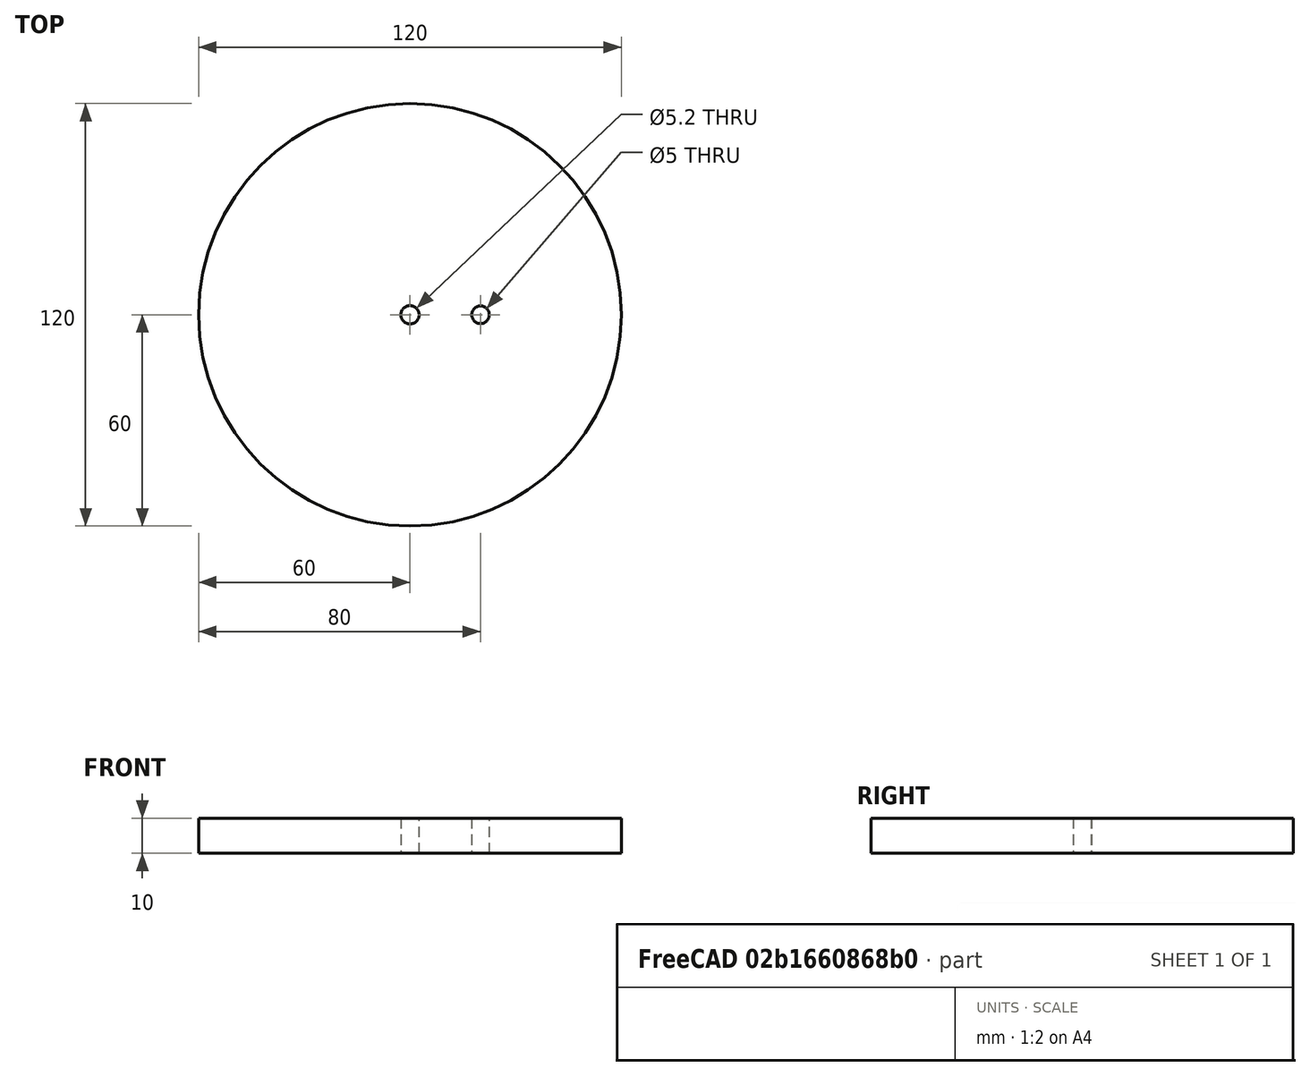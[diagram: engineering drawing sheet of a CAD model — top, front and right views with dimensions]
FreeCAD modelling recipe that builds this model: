
FCSTD DOCUMENT  (FreeCAD 0.21R33771 (Git))
Label: SFT-Mk5-Flywheel
License: Public Domain
LicenseURL: https://en.wikipedia.org/wiki/Public_domain
objects: PartDesign::CoordinateSystem×2, Sketcher::SketchObject×1, Part::Extrusion×1, App::Part×1
note: 4 computed .brp shape members not serialized (recipe doc carries the construction recipe); baked Part::Feature solids carry a one-line shape summary decoded from their .brp

FEATURE [PartDesign::CoordinateSystem] LCS_Origin  label="Axle AP"
  AttacherType = Attacher::AttachEngine3D
  MapMode = 2
  Support = -> [X_Axis]
FEATURE [Sketcher::SketchObject] Sketch
  FullyConstrained = true
  MapMode = 5
  Support = -> [XY_Plane]
  sketch-geometry (3):
    g0: Circle CenterX=0 CenterY=0 CenterZ=0 NormalX=0 NormalY=0 NormalZ=1 AngleXU=0 Radius=60
    g1: Circle CenterX=0 CenterY=0 CenterZ=0 NormalX=0 NormalY=0 NormalZ=1 AngleXU=0 Radius=2.6
    g2: Circle CenterX=20 CenterY=0 CenterZ=0 NormalX=0 NormalY=0 NormalZ=1 AngleXU=0 Radius=2.5
  constraints (7):
    c: Coincident(g0,g-1)
    c: Radius(g0) = 60
    c: Coincident(g1,g0)
    c: Radius(g1) = 2.6
    c: PointOnObject(g2,g-1)
    c: Radius(g2) = 2.5
    c: DistanceX(g2) = 20
FEATURE [Part::Extrusion] Extrude
  Base = -> Sketch
  Dir = (0,0,1)
  DirMode = 2
  FaceMakerClass = Part::FaceMakerBullseye
  LengthFwd = 10
  LengthRev = 0
  Solid = true
  Symmetric = false
FEATURE [PartDesign::CoordinateSystem] Crank_Pin_AP  label="Crank Pin AP"
  AttacherType = Attacher::AttachEngine3D
  MapMode = 11
  Placement = pos=(20,0,0) rot=(0,0,1;1.5708rad)
  Support = -> [Sketch]
FEATURE [App::Part] Flywheel
  Group = -> [LCS_Origin,Sketch,Extrude,Crank_Pin_AP]
  Origin = -> Origin
